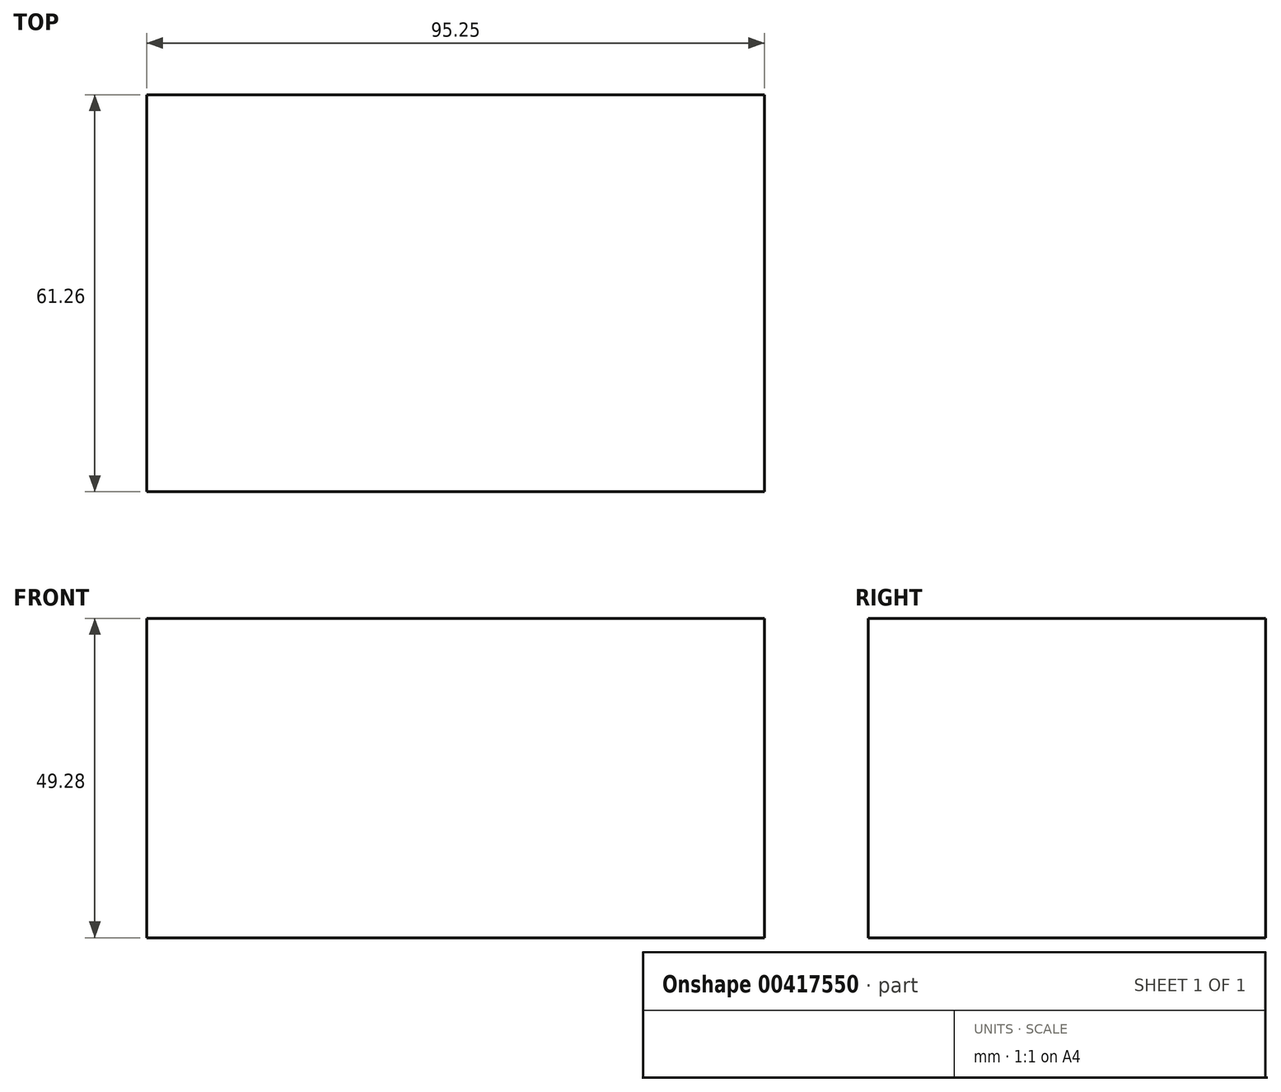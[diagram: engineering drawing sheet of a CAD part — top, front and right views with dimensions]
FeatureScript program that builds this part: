
annotation { "Feature Type Name" : "Feature", "Feature Type Description" : "" }
export const myFeature = defineFeature(function(context is Context, id is Id, definition is map)
    precondition{}
    {
        {
            var Q0;
            Q0=qCreatedBy(makeId("Top.planeOp"),FACE);
            var sketch = newSketch(context, id + "F0", { "sketchPlane" : qUnion([Q0])});
            skLineSegment(sketch, "E0.bottom", {"start": v(-42.21, 25.83) * mm, "end": v(53.04, 25.83) * mm});
            skLineSegment(sketch, "E0.top", {"start": v(-42.21, -35.43) * mm, "end": v(53.04, -35.43) * mm});
            skLineSegment(sketch, "E0.left", {"start": v(-42.21, 25.83) * mm, "end": v(-42.21, -35.43) * mm});
            skLineSegment(sketch, "E0.right", {"start": v(53.04, 25.83) * mm, "end": v(53.04, -35.43) * mm});
            skSolve(sketch);
        }
        {
            var Q0;
            Q0=makeQuery(id+"F0.imprint","IMPRINT",FACE,{"disambiguationData":[TD([[makeQuery(id+"F0.imprint","IMPRINT",EDGE,{"derivedFrom":sQuery(id+"F0.wireOp",EDGE,"E0.bottom")}),-1.0]])]});
            extrude(context, id + "F1", {"entities" : qUnion([Q0]), "offsetDistance" : 25.4 * mm, "depth" : 49.28 * mm});
        }
    });
